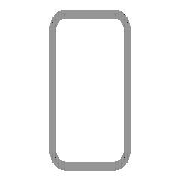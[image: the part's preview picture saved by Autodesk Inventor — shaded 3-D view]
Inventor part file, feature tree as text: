
AUTODESK INVENTOR PART (.ipt)
format: ipt  version: 2025 (Build 290162010, 162A)  size: 133,632 bytes
history: native  units: mm (DEFAULTED — no unit token found)
features: other x4, sketch x1, plane x1
ambient origin geometry x8: Origin, YZ Plane, XZ Plane, XY Plane, X Axis, Y Axis, Z Axis, Center Point
bodies: Solid1 (feature_tree), Body (feature_tree)
feature tree (6):
  parser-record x1  (decoder bookkeeping rows leaked as tree rows — omitted from the tree; the rows remain in map.json)
  other  "Driven Length"
  other  "Start Plane"
  other  "End Plane"
  sketch  "Sketch3"  dims[d3=690.0mm d4=0.0mm d7=6.0mm d9=40.0mm d11=60.0mm d12=3.0mm d13=40.0mm d14=730.0mm d15=20.0mm d16=30.0mm d17=90.0deg d18=690.0mm]
  plane  "Work Plane3"
